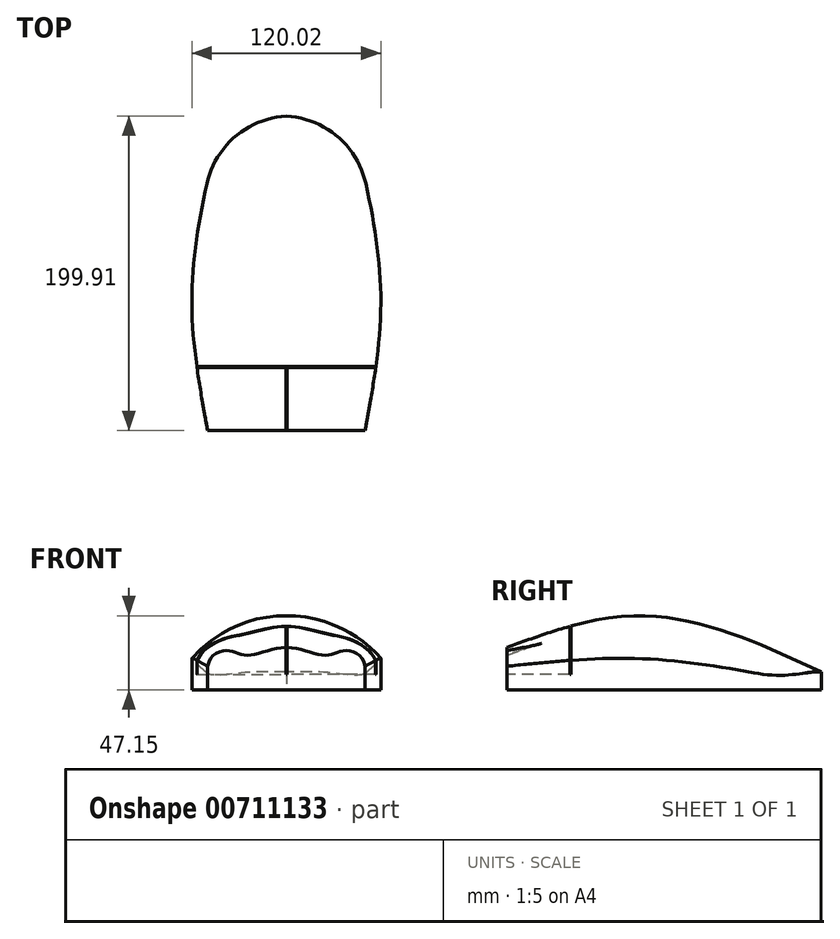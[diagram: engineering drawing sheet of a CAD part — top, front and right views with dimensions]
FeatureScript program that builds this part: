
annotation { "Feature Type Name" : "Feature", "Feature Type Description" : "" }
export const myFeature = defineFeature(function(context is Context, id is Id, definition is map)
    precondition{}
    {
        {
            var Q0;
            Q0=qCreatedBy(makeId("Front.planeOp"),FACE);
            var sketch = newSketch(context, id + "F0", { "sketchPlane" : qUnion([Q0])});
            skLineSegment(sketch, "E0", {"start": v(-40, 0) * mm, "end": v(40, 0) * mm});
            skLineSegment(sketch, "E1", {"start": v(40, 0) * mm, "end": v(40, 2) * mm});
            skLineSegment(sketch, "E2", {"start": v(-40, 0) * mm, "end": v(-40, 2) * mm});
            skArc(sketch, "E3", {"start": v(40, 2) * mm, "mid": v(0, 11.38) * mm, "end": v(-40, 2) * mm});
            skSolve(sketch);
        }
        {
            var Q0;
            Q0=qCreatedBy(makeId("Front.planeOp"),FACE);
            cPlane(context, id + "F1", {"entities" : qUnion([Q0]), "cplaneType" : CPlaneType.OFFSET, "offset" : 120 * mm, "width" : 150 * mm, "height" : 150 * mm});
        }
        {
            var Q0;
            Q0=qCreatedBy(id+"F1.planeOp",FACE);
            cPlane(context, id + "F2", {"entities" : qUnion([Q0]), "cplaneType" : CPlaneType.OFFSET, "offset" : 80 * mm, "width" : 150 * mm, "height" : 150 * mm});
        }
        {
            var Q0;
            Q0=qCreatedBy(id+"F1.planeOp",FACE);
            var sketch = newSketch(context, id + "F3", { "sketchPlane" : qUnion([Q0])});
            skLineSegment(sketch, "E4", {"start": v(-60, 0) * mm, "end": v(60, 0) * mm});
            skLineSegment(sketch, "E5", {"start": v(60, 0) * mm, "end": v(60, 20) * mm});
            skLineSegment(sketch, "E6", {"start": v(-60, 0) * mm, "end": v(-60, 20) * mm});
            skArc(sketch, "E7", {"start": v(60, 20) * mm, "mid": v(0, 47.08) * mm, "end": v(-60, 20) * mm});
            skSolve(sketch);
        }
        {
            var Q0;
            Q0=qCreatedBy(id+"F2.planeOp",FACE);
            var sketch = newSketch(context, id + "F4", { "sketchPlane" : qUnion([Q0])});
            skLineSegment(sketch, "E8", {"start": v(-50, 0) * mm, "end": v(50, 0) * mm});
            skLineSegment(sketch, "E9", {"start": v(50, 0) * mm, "end": v(50, 15) * mm});
            skLineSegment(sketch, "E10", {"start": v(-50, 0) * mm, "end": v(-50, 15) * mm});
            skLineSegment(sketch, "E11", {"start": v(-25, 0) * mm, "end": v(-25, 22) * mm, "construction": true});
            skLineSegment(sketch, "E12", {"start": v(25, 0) * mm, "end": v(25, 22) * mm, "construction": true});
            skLineSegment(sketch, "E13", {"start": v(-37.5, 0) * mm, "end": v(-37.5, 25) * mm, "construction": true});
            skLineSegment(sketch, "E14", {"start": v(37.5, 0) * mm, "end": v(37.5, 25) * mm, "construction": true});
            skFitSpline(sketch, "E15", {"points": [v(-50, 15) * mm, v(-37.5, 25) * mm, v(-25, 22) * mm, v(0, 26.98) * mm, v(25, 22) * mm, v(37.5, 25) * mm, v(50, 15) * mm], "startDerivative": vector(20.98, 139.66) * mm, "endDerivative": vector(18.6, -135.18) * mm});
            skSolve(sketch);
        }
        {
            var Q0;
            Q0=makeQuery(id+"F0.imprint","IMPRINT",FACE,{"disambiguationData":[TD([[makeQuery(id+"F0.imprint","IMPRINT",EDGE,{"derivedFrom":sQuery(id+"F0.wireOp",EDGE,"E0")}),1.0]])]});
            var Q1;
            Q1=makeQuery(id+"F3.imprint","IMPRINT",FACE,{"disambiguationData":[TD([[makeQuery(id+"F3.imprint","IMPRINT",EDGE,{"derivedFrom":sQuery(id+"F3.wireOp",EDGE,"E4")}),1.0]])]});
            var Q2;
            Q2=makeQuery(id+"F4.imprint","IMPRINT",FACE,{"disambiguationData":[TD([[makeQuery(id+"F4.imprint","IMPRINT",EDGE,{"derivedFrom":sQuery(id+"F4.wireOp",EDGE,"E8")}),1.0]])]});
            loft(context, id + "F5", {"sheetProfilesArray" : [{ "sheetProfileEntities" : qUnion([Q0]) }, { "sheetProfileEntities" : qUnion([Q1]) }, { "sheetProfileEntities" : qUnion([Q2]) }]});
        }
        {
            var Q0;
            Q0=makeQuery(id+"F5.opLoft","MID_CAP_EDGE",EDGE,{"disambiguationData":[OSD([sQuery(id+"F0.wireOp",EDGE,"E0"),sQuery(id+"F0.wireOp",EDGE,"E2"),sQuery(id+"F0.wireOp",EDGE,"E3")])],"capPos":0.0});
            fillet(context, id + "F6", {"entities" : qUnion([Q0]), "radius" : 55 * mm, "tangentPropagation" : true, "allowEdgeOverflow" : false});
        }
        {
            var Q0;
            Q0=makeQuery(id+"F5.opLoft","MID_CAP_EDGE",EDGE,{"disambiguationData":[OSD([sQuery(id+"F0.wireOp",EDGE,"E0"),sQuery(id+"F0.wireOp",EDGE,"E1"),sQuery(id+"F0.wireOp",EDGE,"E3")])],"capPos":0.0});
            fillet(context, id + "F7", {"entities" : qUnion([Q0]), "radius" : 55 * mm, "tangentPropagation" : true, "allowEdgeOverflow" : false});
        }
        {
            var Q0;
            Q0=qCreatedBy(id+"F2.planeOp",FACE);
            var sketch = newSketch(context, id + "F8", { "sketchPlane" : qUnion([Q0])});
            skLineSegment(sketch, "E16", {"start": v(0, 0) * mm, "end": v(0, 10) * mm, "construction": true});
            skLineSegment(sketch, "E17.bottom", {"start": v(-0.35, 10) * mm, "end": v(0.35, 10) * mm});
            skLineSegment(sketch, "E17.top", {"start": v(-0.35, 44) * mm, "end": v(0.35, 44) * mm});
            skLineSegment(sketch, "E17.left", {"start": v(-0.35, 10) * mm, "end": v(-0.35, 44) * mm});
            skLineSegment(sketch, "E17.right", {"start": v(0.35, 10) * mm, "end": v(0.35, 44) * mm});
            skSolve(sketch);
        }
        {
            var Q0;
            Q0=makeQuery(id+"F8.imprint","IMPRINT",FACE,{"disambiguationData":[TD([[makeQuery(id+"F8.imprint","IMPRINT",EDGE,{"derivedFrom":sQuery(id+"F8.wireOp",EDGE,"E17.bottom")}),1.0]])]});
            extrude(context, id + "F9", {"entities" : qUnion([Q0]), "operationType" : NewBodyOperationType.REMOVE, "oppositeDirection" : true, "depth" : 40 * mm, "offsetDistance" : 25 * mm});
        }
        {
            var Q0;
            Q0=qCreatedBy(makeId("Right.planeOp"),FACE);
            var sketch = newSketch(context, id + "F10", { "sketchPlane" : qUnion([Q0])});
            skLineSegment(sketch, "E18.bottom", {"start": v(-160, 10) * mm, "end": v(-159.3, 10) * mm});
            skLineSegment(sketch, "E18.top", {"start": v(-160, 45) * mm, "end": v(-159.3, 45) * mm});
            skLineSegment(sketch, "E18.left", {"start": v(-160, 10) * mm, "end": v(-160, 45) * mm});
            skLineSegment(sketch, "E18.right", {"start": v(-159.3, 10) * mm, "end": v(-159.3, 45) * mm});
            skLineSegment(sketch, "E19", {"start": v(-161.9, 0) * mm, "end": v(-126.82, 0) * mm, "construction": true});
            skSolve(sketch);
        }
        {
            var Q0;
            Q0 = qSketchRegion(id + "F10", true);
            extrude(context, id + "F11", {"entities" : qUnion([Q0]), "operationType" : NewBodyOperationType.REMOVE, "oppositeDirection" : true, "depth" : 70 * mm, "offsetDistance" : 25 * mm});
        }
        {
            var Q0;
            Q0 = qSketchRegion(id + "F10", true);
            extrude(context, id + "F12", {"entities" : qUnion([Q0]), "operationType" : NewBodyOperationType.REMOVE, "depth" : 70 * mm, "offsetDistance" : 25 * mm});
        }
    });
